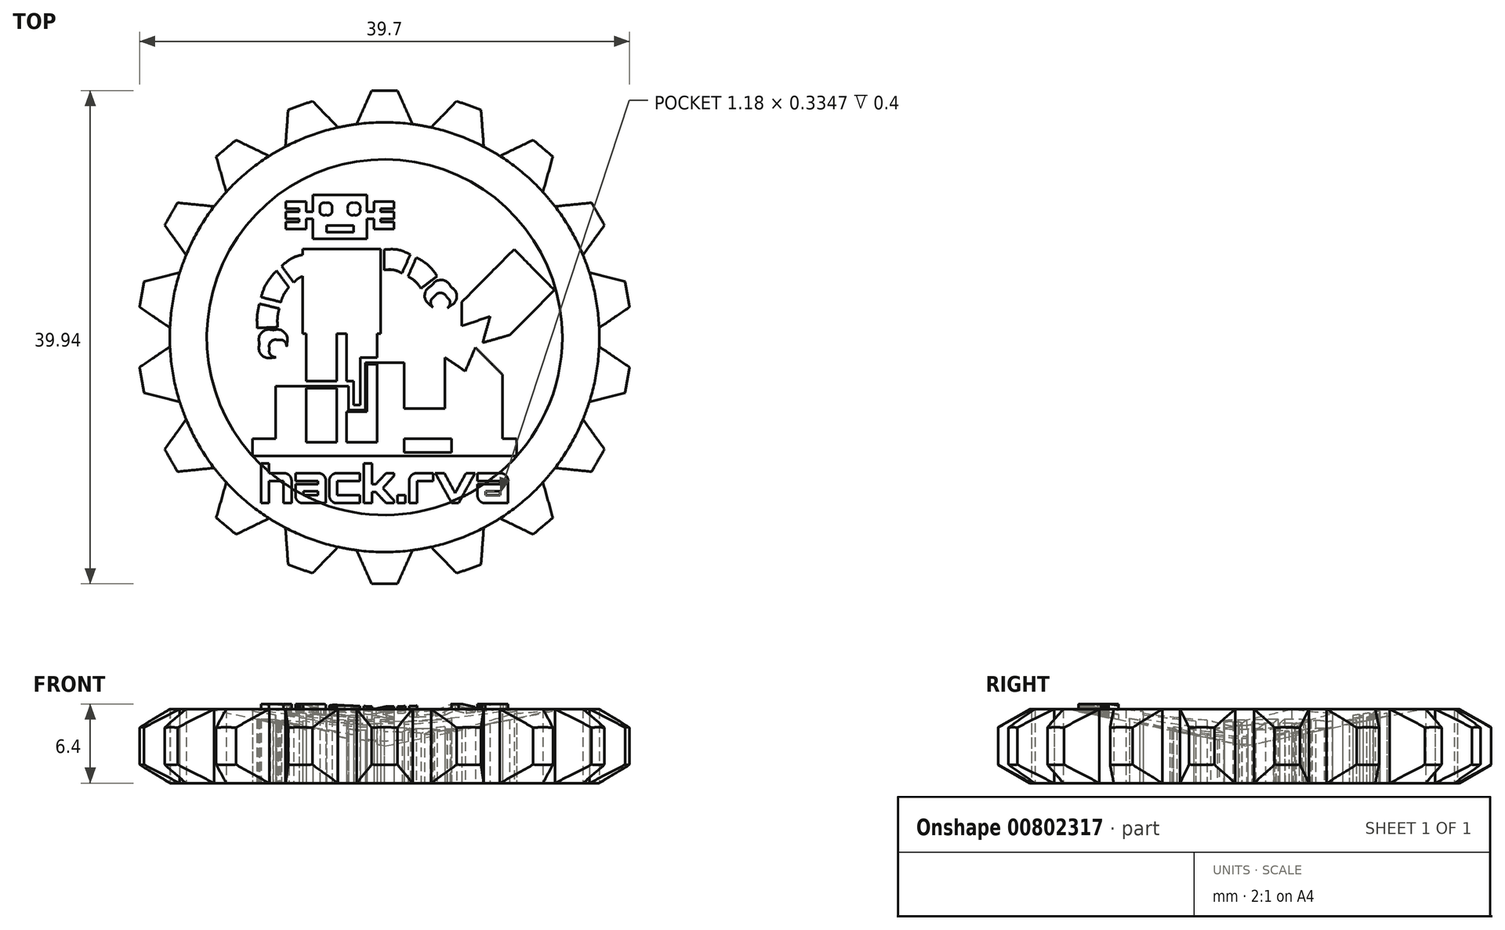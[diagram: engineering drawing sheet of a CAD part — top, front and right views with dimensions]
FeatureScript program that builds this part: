
annotation { "Feature Type Name" : "Feature", "Feature Type Description" : "" }
export const myFeature = defineFeature(function(context is Context, id is Id, definition is map)
    precondition{}
    {
        {
            var Q0;
            Q0=qCreatedBy(makeId("Top.planeOp"),FACE);
            var sketch = newSketch(context, id + "F0", { "sketchPlane" : qUnion([Q0])});
            skCircle(sketch, "E0", {"center": v(0, 0) * mm, "radius": 17.4 * mm, "construction": true});
            skCircle(sketch, "E1", {"center": v(0, 0) * mm, "radius": 20 * mm, "construction": true});
            skLineSegment(sketch, "E2", {"start": v(0, 0) * mm, "end": v(0, 27.02) * mm, "construction": true});
            skLineSegment(sketch, "E3", {"start": v(0, 0) * mm, "end": v(-2.84, 21.54) * mm, "construction": true});
            skLineSegment(sketch, "E4", {"start": v(0, 0) * mm, "end": v(-1.42, 27.06) * mm, "construction": true});
            skPoint(sketch, "E4.endSnap0", {"position": v(-1.42, 10.77) * mm});
            skLineSegment(sketch, "E5", {"start": v(-2.27, 17.25) * mm, "end": v(-1.05, 19.97) * mm});
            skLineSegment(sketch, "E6", {"start": v(-1.05, 19.97) * mm, "end": v(0, 19.97) * mm});
            skLineSegment(sketch, "E7.MirrorCS", {"start": v(2.27, 17.25) * mm, "end": v(1.05, 19.97) * mm});
            skLineSegment(sketch, "E8.MirrorCS", {"start": v(1.05, 19.97) * mm, "end": v(0, 19.97) * mm});
            skLineSegment(sketch, "E9", {"start": v(-2.27, 17.25) * mm, "end": v(2.27, 17.25) * mm});
            skSolve(sketch);
        }
        {
            var Q0;
            Q0=qCreatedBy(makeId("Top.planeOp"),FACE);
            var sketch = newSketch(context, id + "F1", { "sketchPlane" : qUnion([Q0])});
            skCircle(sketch, "E10", {"center": v(0, 0) * mm, "radius": 17.4 * mm});
            skSolve(sketch);
        }
        {
            var Q0;
            Q0 = qSketchRegion(id + "F1", true);
            var Q1;
            Q1 = qSketchRegion(id + "F0", true);
            extrude(context, id + "F2", {"entities" : qUnion([Q0, Q1]), "depth" : 6 * mm, "offsetDistance" : 25 * mm});
        }
        {
            var Q0;
            Q0=qCreatedBy(makeId("Front.planeOp"),FACE);
            var sketch = newSketch(context, id + "F3", { "sketchPlane" : qUnion([Q0])});
            skLineSegment(sketch, "E11", {"start": v(0, 0) * mm, "end": v(0, 3) * mm});
            skLineSegment(sketch, "E12", {"start": v(0, 3) * mm, "end": v(-14.4, 6) * mm});
            skLineSegment(sketch, "E13", {"start": v(-14.4, 6) * mm, "end": v(-17.4, 6) * mm});
            skLineSegment(sketch, "E14", {"start": v(-17.4, 6) * mm, "end": v(-20, 4.5) * mm});
            skLineSegment(sketch, "E15", {"start": v(-20, 4.5) * mm, "end": v(-20, 1.5) * mm});
            skLineSegment(sketch, "E16", {"start": v(-20, 1.5) * mm, "end": v(-17.4, 0) * mm});
            skLineSegment(sketch, "E17", {"start": v(-17.4, 0) * mm, "end": v(0, 0) * mm});
            skSolve(sketch);
        }
        {
            var Q0;
            Q0=makeQuery(id+"F2.opExtrude","SWEPT_BODY",BODY,{"disambiguationData":[OSD([sQuery(id+"F0.wireOp",EDGE,"E5"),sQuery(id+"F0.wireOp",EDGE,"E6"),sQuery(id+"F0.wireOp",EDGE,"E7.MirrorCS"),sQuery(id+"F0.wireOp",EDGE,"E8.MirrorCS"),sQuery(id+"F0.wireOp",EDGE,"E9")])]});
            var Q1;
            Q1=sQuery(id+"F3.wireOp",EDGE,"E11");
            circularPattern(context, id + "F4", {"operationType" : NewBodyOperationType.ADD, "entities" : qUnion([Q0]), "axis" : qUnion([Q1]), "angle" : 360 * degree, "instanceCount" : 18, "equalSpace" : true});
        }
        {
            var Q0;
            Q0=qCreatedBy(makeId("Top.planeOp"),FACE);
            var sketch = newSketch(context, id + "F5", { "sketchPlane" : qUnion([Q0])});
            skLineSegment(sketch, "E18", {"start": v(7.36, -0.83) * mm, "end": v(6.54, -2.75) * mm});
            skLineSegment(sketch, "E19", {"start": v(6.54, -2.75) * mm, "end": v(4.9, -1.65) * mm});
            skLineSegment(sketch, "E20", {"start": v(4.9, -1.65) * mm, "end": v(4.9, -9.06) * mm});
            skLineSegment(sketch, "E21", {"start": v(4.9, -9.06) * mm, "end": v(9.56, -9.06) * mm});
            skLineSegment(sketch, "E22", {"start": v(9.56, -9.06) * mm, "end": v(9.56, -3.02) * mm});
            skLineSegment(sketch, "E23", {"start": v(9.56, -3.02) * mm, "end": v(8.46, -1.92) * mm});
            skLineSegment(sketch, "E24", {"start": v(8.46, -1.92) * mm, "end": v(7.36, -0.83) * mm});
            skLineSegment(sketch, "E25", {"start": v(1.6, -5.77) * mm, "end": v(5.44, -5.77) * mm});
            skLineSegment(sketch, "E26", {"start": v(5.44, -5.77) * mm, "end": v(5.44, -9.33) * mm});
            skLineSegment(sketch, "E27", {"start": v(5.44, -9.33) * mm, "end": v(1.6, -9.33) * mm});
            skLineSegment(sketch, "E28", {"start": v(1.6, -9.33) * mm, "end": v(1.6, -5.77) * mm});
            skLineSegment(sketch, "E29", {"start": v(8.55, 1.69) * mm, "end": v(7.95, -0.45) * mm});
            skLineSegment(sketch, "E30", {"start": v(7.95, -0.45) * mm, "end": v(10.12, 0.17) * mm});
            skLineSegment(sketch, "E31", {"start": v(10.12, 0.17) * mm, "end": v(13.76, 3.82) * mm});
            skLineSegment(sketch, "E32", {"start": v(13.76, 3.82) * mm, "end": v(10.5, 7.12) * mm});
            skLineSegment(sketch, "E33", {"start": v(10.5, 7.12) * mm, "end": v(6.26, 2.85) * mm});
            skLineSegment(sketch, "E34", {"start": v(6.26, 2.85) * mm, "end": v(6.26, 0.9) * mm});
            skLineSegment(sketch, "E35", {"start": v(6.26, 0.9) * mm, "end": v(8.55, 1.69) * mm});
            skFitSpline(sketch, "E36", {"points": [v(-9.33, -0.94) * mm, v(-9.33, -0.55) * mm, v(-9.02, -0.23) * mm, v(-8.62, -0.23) * mm]});
            skFitSpline(sketch, "E37", {"points": [v(-8.62, -0.23) * mm, v(-8.3, -0.23) * mm, v(-8.02, -0.46) * mm, v(-7.94, -0.77) * mm]});
            skFitSpline(sketch, "E38", {"points": [v(-7.94, -0.77) * mm, v(-7.92, -0.7) * mm, v(-7.91, -0.61) * mm, v(-7.91, -0.53) * mm]});
            skFitSpline(sketch, "E39", {"points": [v(-7.91, -0.53) * mm, v(-7.91, 0.08) * mm, v(-8.41, 0.58) * mm, v(-9.03, 0.58) * mm]});
            skFitSpline(sketch, "E40", {"points": [v(-9.03, 0.58) * mm, v(-9.64, 0.58) * mm, v(-10.14, 0.08) * mm, v(-10.14, -0.53) * mm]});
            skFitSpline(sketch, "E41", {"points": [v(-10.14, -0.53) * mm, v(-10.14, -1.15) * mm, v(-9.64, -1.65) * mm, v(-9.03, -1.65) * mm]});
            skFitSpline(sketch, "E42", {"points": [v(-9.03, -1.65) * mm, v(-8.95, -1.65) * mm, v(-8.87, -1.64) * mm, v(-8.8, -1.63) * mm]});
            skFitSpline(sketch, "E43", {"points": [v(-8.8, -1.63) * mm, v(-9.1, -1.55) * mm, v(-9.33, -1.27) * mm, v(-9.33, -0.94) * mm]});
            skLineSegment(sketch, "E44", {"start": v(-1.42, 10.15) * mm, "end": v(0.77, 10.15) * mm});
            skLineSegment(sketch, "E45", {"start": v(0.77, 10.15) * mm, "end": v(0.77, 9.6) * mm});
            skLineSegment(sketch, "E46", {"start": v(0.77, 9.6) * mm, "end": v(-1.42, 9.6) * mm});
            skLineSegment(sketch, "E47", {"start": v(-1.42, 9.6) * mm, "end": v(-1.42, 10.15) * mm});
            skFitSpline(sketch, "E48", {"points": [v(4.04, 3.29) * mm, v(4.33, 3.55) * mm, v(4.78, 3.53) * mm, v(5.04, 3.24) * mm]});
            skFitSpline(sketch, "E49", {"points": [v(5.04, 3.24) * mm, v(5.27, 3) * mm, v(5.29, 2.64) * mm, v(5.11, 2.38) * mm]});
            skFitSpline(sketch, "E50", {"points": [v(5.11, 2.38) * mm, v(5.18, 2.42) * mm, v(5.24, 2.46) * mm, v(5.3, 2.51) * mm]});
            skFitSpline(sketch, "E51", {"points": [v(5.3, 2.51) * mm, v(5.75, 2.93) * mm, v(5.79, 3.64) * mm, v(5.37, 4.1) * mm]});
            skFitSpline(sketch, "E52", {"points": [v(5.37, 4.1) * mm, v(4.95, 4.55) * mm, v(4.25, 4.58) * mm, v(3.8, 4.16) * mm]});
            skFitSpline(sketch, "E53", {"points": [v(3.8, 4.16) * mm, v(3.34, 3.75) * mm, v(3.3, 3.04) * mm, v(3.72, 2.58) * mm]});
            skFitSpline(sketch, "E54", {"points": [v(3.72, 2.58) * mm, v(3.78, 2.53) * mm, v(3.84, 2.48) * mm, v(3.9, 2.43) * mm]});
            skFitSpline(sketch, "E55", {"points": [v(3.9, 2.43) * mm, v(3.75, 2.71) * mm, v(3.8, 3.07) * mm, v(4.04, 3.29) * mm]});
            skFitSpline(sketch, "E56", {"points": [v(-5.24, 10.39) * mm, v(-5.24, 10.65) * mm, v(-5.02, 10.87) * mm, v(-4.75, 10.87) * mm]});
            skFitSpline(sketch, "E57", {"points": [v(-4.75, 10.87) * mm, v(-4.48, 10.87) * mm, v(-4.26, 10.65) * mm, v(-4.26, 10.39) * mm]});
            skFitSpline(sketch, "E58", {"points": [v(-4.26, 10.39) * mm, v(-4.26, 10.12) * mm, v(-4.48, 9.9) * mm, v(-4.75, 9.9) * mm]});
            skFitSpline(sketch, "E59", {"points": [v(-4.75, 9.9) * mm, v(-5.02, 9.9) * mm, v(-5.24, 10.12) * mm, v(-5.24, 10.39) * mm]});
            skLineSegment(sketch, "E60", {"start": v(-5.81, 11.52) * mm, "end": v(-5.81, 7.95) * mm});
            skLineSegment(sketch, "E61", {"start": v(-5.81, 7.95) * mm, "end": v(-1.42, 7.95) * mm});
            skLineSegment(sketch, "E62", {"start": v(-1.42, 7.95) * mm, "end": v(-1.42, 11.52) * mm});
            skLineSegment(sketch, "E63", {"start": v(-1.42, 11.52) * mm, "end": v(-5.81, 11.52) * mm});
            skFitSpline(sketch, "E64", {"points": [v(-2.48, 9.9) * mm, v(-2.75, 9.9) * mm, v(-2.97, 10.12) * mm, v(-2.97, 10.39) * mm]});
            skFitSpline(sketch, "E65", {"points": [v(-2.97, 10.39) * mm, v(-2.97, 10.65) * mm, v(-2.75, 10.87) * mm, v(-2.48, 10.87) * mm]});
            skFitSpline(sketch, "E66", {"points": [v(-2.48, 10.87) * mm, v(-2.21, 10.87) * mm, v(-2, 10.65) * mm, v(-2, 10.39) * mm]});
            skFitSpline(sketch, "E67", {"points": [v(-2, 10.39) * mm, v(-2, 10.12) * mm, v(-2.21, 9.9) * mm, v(-2.48, 9.9) * mm]});
            skLineSegment(sketch, "E68", {"start": v(-2.52, 8.5) * mm, "end": v(-4.71, 8.5) * mm});
            skLineSegment(sketch, "E69", {"start": v(-4.71, 8.5) * mm, "end": v(-4.71, 9.05) * mm});
            skLineSegment(sketch, "E70", {"start": v(-4.71, 9.05) * mm, "end": v(-2.52, 9.05) * mm});
            skLineSegment(sketch, "E71", {"start": v(-2.52, 9.05) * mm, "end": v(-2.52, 8.5) * mm});
            skLineSegment(sketch, "E72", {"start": v(0.77, 8.78) * mm, "end": v(-0.87, 8.78) * mm});
            skLineSegment(sketch, "E73", {"start": v(-0.87, 8.78) * mm, "end": v(-0.87, 10.97) * mm});
            skLineSegment(sketch, "E74", {"start": v(-0.87, 10.97) * mm, "end": v(0.77, 10.97) * mm});
            skLineSegment(sketch, "E75", {"start": v(0.77, 10.97) * mm, "end": v(0.77, 10.42) * mm});
            skLineSegment(sketch, "E76", {"start": v(0.77, 10.42) * mm, "end": v(-0.32, 10.42) * mm});
            skLineSegment(sketch, "E77", {"start": v(-0.32, 10.42) * mm, "end": v(-0.32, 9.33) * mm});
            skLineSegment(sketch, "E78", {"start": v(-0.32, 9.33) * mm, "end": v(0.77, 9.33) * mm});
            skLineSegment(sketch, "E79", {"start": v(0.77, 9.33) * mm, "end": v(0.77, 8.78) * mm});
            skLineSegment(sketch, "E80", {"start": v(-8, 10.15) * mm, "end": v(-5.81, 10.15) * mm});
            skLineSegment(sketch, "E81", {"start": v(-5.81, 10.15) * mm, "end": v(-5.81, 9.6) * mm});
            skLineSegment(sketch, "E82", {"start": v(-5.81, 9.6) * mm, "end": v(-8, 9.6) * mm});
            skLineSegment(sketch, "E83", {"start": v(-8, 9.6) * mm, "end": v(-8, 10.15) * mm});
            skLineSegment(sketch, "E84", {"start": v(-6.36, 8.78) * mm, "end": v(-8, 8.78) * mm});
            skLineSegment(sketch, "E85", {"start": v(-8, 8.78) * mm, "end": v(-8, 9.33) * mm});
            skLineSegment(sketch, "E86", {"start": v(-8, 9.33) * mm, "end": v(-6.9, 9.33) * mm});
            skLineSegment(sketch, "E87", {"start": v(-6.9, 9.33) * mm, "end": v(-6.9, 10.42) * mm});
            skLineSegment(sketch, "E88", {"start": v(-6.9, 10.42) * mm, "end": v(-8, 10.42) * mm});
            skLineSegment(sketch, "E89", {"start": v(-8, 10.42) * mm, "end": v(-8, 10.97) * mm});
            skLineSegment(sketch, "E90", {"start": v(-8, 10.97) * mm, "end": v(-6.36, 10.97) * mm});
            skLineSegment(sketch, "E91", {"start": v(-6.36, 10.97) * mm, "end": v(-6.36, 8.78) * mm});
            skLineSegment(sketch, "E92", {"start": v(-6.63, 7.13) * mm, "end": v(-0.32, 7.13) * mm});
            skLineSegment(sketch, "E93", {"start": v(-0.32, 7.13) * mm, "end": v(-0.32, 0.27) * mm});
            skLineSegment(sketch, "E94", {"start": v(-0.32, 0.27) * mm, "end": v(-6.63, 0.27) * mm});
            skLineSegment(sketch, "E95", {"start": v(-6.63, 0.27) * mm, "end": v(-6.63, 7.13) * mm});
            skFitSpline(sketch, "E96", {"points": [v(1.9, 4.93) * mm, v(2.29, 4.69) * mm, v(2.64, 4.36) * mm, v(2.95, 3.95) * mm]});
            skLineSegment(sketch, "E97", {"start": v(2.58, 6.45) * mm, "end": v(1.9, 4.93) * mm});
            skLineSegment(sketch, "E98", {"start": v(1.9, 4.93) * mm, "end": v(2.58, 6.45) * mm});
            skFitSpline(sketch, "E99", {"points": [v(4.26, 4.95) * mm, v(3.78, 5.59) * mm, v(3.2, 6.1) * mm, v(2.58, 6.45) * mm]});
            skLineSegment(sketch, "E100", {"start": v(2.95, 3.95) * mm, "end": v(4.26, 4.95) * mm});
            skLineSegment(sketch, "E101", {"start": v(4.26, 4.95) * mm, "end": v(2.95, 3.95) * mm});
            skFitSpline(sketch, "E102", {"points": [v(-5.82, 6.69) * mm, v(-6.77, 6.65) * mm, v(-7.63, 6.32) * mm, v(-8.34, 5.76) * mm]});
            skFitSpline(sketch, "E103", {"points": [v(-7.37, 4.43) * mm, v(-6.91, 4.8) * mm, v(-6.37, 5.02) * mm, v(-5.75, 5.04) * mm]});
            skFitSpline(sketch, "E104", {"points": [v(-5.75, 5.04) * mm, v(-4.6, 5.1) * mm, v(-3.52, 4.48) * mm, v(-2.78, 3.35) * mm]});
            skLineSegment(sketch, "E105", {"start": v(-8.34, 5.76) * mm, "end": v(-7.37, 4.43) * mm});
            skLineSegment(sketch, "E106", {"start": v(-7.37, 4.43) * mm, "end": v(-8.34, 5.76) * mm});
            skFitSpline(sketch, "E107", {"points": [v(-1.4, 4.25) * mm, v(-2.47, 5.88) * mm, v(-4.08, 6.77) * mm, v(-5.82, 6.69) * mm]});
            skLineSegment(sketch, "E108", {"start": v(-2.78, 3.35) * mm, "end": v(-1.4, 4.25) * mm});
            skLineSegment(sketch, "E109", {"start": v(-1.4, 4.25) * mm, "end": v(-2.78, 3.35) * mm});
            skFitSpline(sketch, "E110", {"points": [v(-10.14, 2.71) * mm, v(-10.28, 2.1) * mm, v(-10.34, 1.43) * mm, v(-10.3, 0.74) * mm]});
            skLineSegment(sketch, "E111", {"start": v(-8.54, 2.32) * mm, "end": v(-10.14, 2.71) * mm});
            skLineSegment(sketch, "E112", {"start": v(-10.14, 2.71) * mm, "end": v(-8.54, 2.32) * mm});
            skFitSpline(sketch, "E113", {"points": [v(-8.66, 0.82) * mm, v(-8.69, 1.35) * mm, v(-8.64, 1.85) * mm, v(-8.54, 2.32) * mm]});
            skLineSegment(sketch, "E114", {"start": v(-10.3, 0.74) * mm, "end": v(-8.66, 0.82) * mm});
            skLineSegment(sketch, "E115", {"start": v(-8.66, 0.82) * mm, "end": v(-10.3, 0.74) * mm});
            skFitSpline(sketch, "E116", {"points": [v(-8.4, 2.85) * mm, v(-8.28, 3.22) * mm, v(-8.12, 3.55) * mm, v(-7.92, 3.84) * mm]});
            skFitSpline(sketch, "E117", {"points": [v(-7.92, 3.84) * mm, v(-7.87, 3.9) * mm, v(-7.81, 3.98) * mm, v(-7.76, 4.04) * mm]});
            skFitSpline(sketch, "E118", {"points": [v(-8.75, 5.39) * mm, v(-8.94, 5.2) * mm, v(-9.11, 5) * mm, v(-9.27, 4.78) * mm]});
            skFitSpline(sketch, "E119", {"points": [v(-9.27, 4.78) * mm, v(-9.58, 4.32) * mm, v(-9.82, 3.8) * mm, v(-10, 3.24) * mm]});
            skLineSegment(sketch, "E120", {"start": v(-7.76, 4.04) * mm, "end": v(-8.75, 5.39) * mm});
            skLineSegment(sketch, "E121", {"start": v(-8.75, 5.39) * mm, "end": v(-7.76, 4.04) * mm});
            skLineSegment(sketch, "E122", {"start": v(-10, 3.24) * mm, "end": v(-8.4, 2.85) * mm});
            skLineSegment(sketch, "E123", {"start": v(-8.4, 2.85) * mm, "end": v(-10, 3.24) * mm});
            skLineSegment(sketch, "E124", {"start": v(1.6, -2.05) * mm, "end": v(-1.57, -2.05) * mm});
            skLineSegment(sketch, "E125", {"start": v(-2.52, -3.57) * mm, "end": v(-2.52, -5.5) * mm});
            skLineSegment(sketch, "E126", {"start": v(-2.52, -5.5) * mm, "end": v(-1.97, -5.5) * mm});
            skLineSegment(sketch, "E127", {"start": v(-0.6, -1.65) * mm, "end": v(-0.6, 1.1) * mm});
            skLineSegment(sketch, "E128", {"start": v(-0.6, 1.1) * mm, "end": v(-3.07, 1.1) * mm});
            skLineSegment(sketch, "E129", {"start": v(-3.07, 1.1) * mm, "end": v(-3.07, -3.57) * mm});
            skLineSegment(sketch, "E130", {"start": v(-3.07, -3.57) * mm, "end": v(-2.52, -3.57) * mm});
            skLineSegment(sketch, "E131", {"start": v(-0.6, -2.2) * mm, "end": v(-1.42, -2.2) * mm});
            skLineSegment(sketch, "E132", {"start": v(-1.42, -2.2) * mm, "end": v(-1.42, -6.04) * mm});
            skLineSegment(sketch, "E133", {"start": v(-1.42, -6.04) * mm, "end": v(-3.07, -6.04) * mm});
            skLineSegment(sketch, "E134", {"start": v(-3.07, -6.04) * mm, "end": v(-3.07, -8.5) * mm});
            skLineSegment(sketch, "E135", {"start": v(-3.07, -8.5) * mm, "end": v(-1.15, -8.5) * mm});
            skLineSegment(sketch, "E136", {"start": v(-1.15, -8.5) * mm, "end": v(-0.6, -8.5) * mm});
            skLineSegment(sketch, "E137", {"start": v(-0.6, -8.5) * mm, "end": v(-0.6, -2.2) * mm});
            skLineSegment(sketch, "E138", {"start": v(-10.7, -8.23) * mm, "end": v(10.7, -8.23) * mm});
            skLineSegment(sketch, "E139", {"start": v(10.7, -9.6) * mm, "end": v(-10.7, -9.6) * mm});
            skFitSpline(sketch, "E140", {"points": [v(-0.05, 5.44) * mm, v(0.45, 5.48) * mm, v(0.95, 5.4) * mm, v(1.42, 5.2) * mm]});
            skLineSegment(sketch, "E141", {"start": v(-0.05, 7.09) * mm, "end": v(-0.05, 5.44) * mm});
            skLineSegment(sketch, "E142", {"start": v(-0.05, 5.44) * mm, "end": v(-0.05, 7.09) * mm});
            skFitSpline(sketch, "E143", {"points": [v(2.09, 6.7) * mm, v(1.41, 7) * mm, v(0.7, 7.13) * mm, v(-0.05, 7.09) * mm]});
            skLineSegment(sketch, "E144", {"start": v(1.42, 5.2) * mm, "end": v(2.09, 6.7) * mm});
            skLineSegment(sketch, "E145", {"start": v(2.09, 6.7) * mm, "end": v(1.42, 5.2) * mm});
            skLineSegment(sketch, "E146", {"start": v(-6.36, 1.1) * mm, "end": v(-3.89, 1.1) * mm});
            skLineSegment(sketch, "E147", {"start": v(-3.89, 1.1) * mm, "end": v(-3.89, -3.57) * mm});
            skLineSegment(sketch, "E148", {"start": v(-3.89, -3.57) * mm, "end": v(-6.36, -3.57) * mm});
            skLineSegment(sketch, "E149", {"start": v(-6.36, -3.57) * mm, "end": v(-6.36, 1.1) * mm});
            skLineSegment(sketch, "E150", {"start": v(-6.36, -4.12) * mm, "end": v(-3.89, -4.12) * mm});
            skLineSegment(sketch, "E151", {"start": v(-3.89, -4.12) * mm, "end": v(-3.89, -8.5) * mm});
            skLineSegment(sketch, "E152", {"start": v(-3.89, -8.5) * mm, "end": v(-6.36, -8.5) * mm});
            skLineSegment(sketch, "E153", {"start": v(-6.36, -8.5) * mm, "end": v(-6.36, -4.12) * mm});
            skLineSegment(sketch, "E154", {"start": v(10.7, -8.23) * mm, "end": v(10.7, -9.6) * mm});
            skLineSegment(sketch, "E155", {"start": v(-10.7, -9.6) * mm, "end": v(-10.7, -8.23) * mm});
            skLineSegment(sketch, "E156", {"start": v(-1.57, -2.05) * mm, "end": v(-1.57, -5.9) * mm});
            skLineSegment(sketch, "E157", {"start": v(-1.97, -1.65) * mm, "end": v(-1.97, -5.5) * mm});
            skLineSegment(sketch, "E158", {"start": v(1.6, -2.05) * mm, "end": v(1.6, -8.78) * mm});
            skLineSegment(sketch, "E159", {"start": v(1.6, -8.78) * mm, "end": v(-0.87, -8.78) * mm});
            skLineSegment(sketch, "E160", {"start": v(-0.87, -8.78) * mm, "end": v(-0.87, -9.33) * mm});
            skLineSegment(sketch, "E161", {"start": v(-0.87, -9.33) * mm, "end": v(-2.8, -9.33) * mm});
            skLineSegment(sketch, "E162", {"start": v(-2.8, -9.33) * mm, "end": v(-2.8, -9.6) * mm});
            skLineSegment(sketch, "E163", {"start": v(-2.8, -9.6) * mm, "end": v(-8.83, -9.6) * mm});
            skLineSegment(sketch, "E164", {"start": v(-8.83, -9.6) * mm, "end": v(-8.83, -3.97) * mm});
            skLineSegment(sketch, "E165", {"start": v(-0.6, -1.65) * mm, "end": v(-1.97, -1.65) * mm});
            skLineSegment(sketch, "E166", {"start": v(-2.92, -5.9) * mm, "end": v(-1.57, -5.9) * mm});
            skLineSegment(sketch, "E167", {"start": v(-2.92, -3.97) * mm, "end": v(-2.92, -5.9) * mm});
            skLineSegment(sketch, "E168", {"start": v(-2.92, -3.97) * mm, "end": v(-8.83, -3.97) * mm});
            skSolve(sketch);
        }
        {
            var Q0;
            Q0 = qSketchRegion(id + "F5", true);
            var Q1;
            Q1=sQuery(id+"F5.wireOp",EDGE,"E134");
            var Q2;
            Q2=sQuery(id+"F5.wireOp",EDGE,"E94");
            var Q3;
            Q3=sQuery(id+"F5.wireOp",EDGE,"E148");
            var Q4;
            Q4=sQuery(id+"F5.wireOp",EDGE,"E99");
            var Q5;
            Q5=sQuery(id+"F5.wireOp",EDGE,"E143");
            var Q6;
            Q6=sQuery(id+"F5.wireOp",EDGE,"E22");
            var Q7;
            Q7=sQuery(id+"F5.wireOp",EDGE,"E35");
            var Q8;
            Q8=sQuery(id+"F5.wireOp",EDGE,"E28");
            var Q9;
            Q9=sQuery(id+"F5.wireOp",EDGE,"E110");
            var Q10;
            Q10=sQuery(id+"F5.wireOp",EDGE,"95198ed3-3c3b-4ae5-9471-770df729d098");
            var Q11;
            Q11=sQuery(id+"F5.wireOp",EDGE,"E149");
            var Q12;
            Q12=sQuery(id+"F5.wireOp",EDGE,"E137");
            var Q13;
            Q13=sQuery(id+"F5.wireOp",EDGE,"E26");
            var Q14;
            Q14=sQuery(id+"F5.wireOp",EDGE,"E104");
            var Q15;
            Q15=sQuery(id+"F5.wireOp",EDGE,"E20");
            var Q16;
            Q16=sQuery(id+"F5.wireOp",EDGE,"E68");
            var Q17;
            Q17=sQuery(id+"F5.wireOp",EDGE,"E138");
            var Q18;
            Q18=sQuery(id+"F5.wireOp",EDGE,"E129");
            var Q19;
            Q19=sQuery(id+"F5.wireOp",EDGE,"77c6bc89-9393-4709-9f76-2ba73c08c8e3");
            var Q20;
            Q20=sQuery(id+"F5.wireOp",EDGE,"E34");
            var Q21;
            Q21=sQuery(id+"F5.wireOp",EDGE,"E147");
            var Q22;
            Q22=sQuery(id+"F5.wireOp",EDGE,"b3271c8d-d34e-48d3-8350-166866a1ef0d");
            var Q23;
            Q23=sQuery(id+"F5.wireOp",EDGE,"E33");
            var Q24;
            Q24=sQuery(id+"F5.wireOp",EDGE,"E152");
            var Q25;
            Q25=sQuery(id+"F5.wireOp",EDGE,"E21");
            var Q26;
            Q26=sQuery(id+"F5.wireOp",EDGE,"9cf7919e-c9ea-4169-a484-167db1e63cf2");
            var Q27;
            Q27=sQuery(id+"F5.wireOp",EDGE,"E70");
            var Q28;
            Q28=sQuery(id+"F5.wireOp",EDGE,"E18");
            var Q29;
            Q29=sQuery(id+"F5.wireOp",EDGE,"E31");
            var Q30;
            Q30=sQuery(id+"F5.wireOp",EDGE,"E32");
            var Q31;
            Q31=sQuery(id+"F5.wireOp",EDGE,"E27");
            var Q32;
            Q32=sQuery(id+"F5.wireOp",EDGE,"E30");
            var Q33;
            Q33=sQuery(id+"F5.wireOp",EDGE,"E29");
            var Q34;
            Q34=sQuery(id+"F5.wireOp",EDGE,"E153");
            var Q35;
            Q35=sQuery(id+"F5.wireOp",EDGE,"E107");
            var Q36;
            Q36=sQuery(id+"F5.wireOp",EDGE,"E127");
            var Q37;
            Q37=sQuery(id+"F5.wireOp",EDGE,"E124");
            var Q38;
            Q38=sQuery(id+"F5.wireOp",EDGE,"E92");
            var Q39;
            Q39=sQuery(id+"F5.wireOp",EDGE,"E150");
            var Q40;
            Q40=sQuery(id+"F5.wireOp",EDGE,"E102");
            var Q41;
            Q41=sQuery(id+"F5.wireOp",EDGE,"1cbca8c9-4c5e-4ba1-ad6a-0479403318c5");
            var Q42;
            Q42=sQuery(id+"F5.wireOp",EDGE,"E151");
            var Q43;
            Q43=sQuery(id+"F5.wireOp",EDGE,"E25");
            var Q44;
            Q44=sQuery(id+"F5.wireOp",EDGE,"E146");
            var Q45;
            Q45=sQuery(id+"F5.wireOp",EDGE,"E132");
            var Q46;
            Q46=sQuery(id+"F5.wireOp",EDGE,"9599e65c-5a11-434d-bada-090ac9876402");
            var Q47;
            Q47=sQuery(id+"F5.wireOp",EDGE,"E63");
            var Q48;
            Q48=sQuery(id+"F5.wireOp",EDGE,"E95");
            var Q49;
            Q49=sQuery(id+"F5.wireOp",EDGE,"3e5a58c2-594a-425e-9fb5-5e991799c867");
            var Q50;
            Q50=sQuery(id+"F5.wireOp",EDGE,"E93");
            var Q51;
            Q51=sQuery(id+"F5.wireOp",EDGE,"E61");
            var Q52;
            Q52=sQuery(id+"F5.wireOp",EDGE,"E128");
            var Q53;
            Q53=sQuery(id+"F5.wireOp",EDGE,"E139");
            var Q54;
            Q54=sQuery(id+"F5.wireOp",EDGE,"9c611efc-dcd8-4982-9a14-8ccc37464665");
            var Q55;
            Q55=sQuery(id+"F5.wireOp",EDGE,"E135");
            var Q56;
            Q56=sQuery(id+"F5.wireOp",EDGE,"E67");
            var Q57;
            Q57=sQuery(id+"F5.wireOp",EDGE,"a202889e-5133-40a2-9648-54841ea52ae1");
            var Q58;
            Q58=sQuery(id+"F5.wireOp",EDGE,"E51");
            var Q59;
            Q59=sQuery(id+"F5.wireOp",EDGE,"E52");
            var Q60;
            Q60=sQuery(id+"F5.wireOp",EDGE,"E23");
            var Q61;
            Q61=sQuery(id+"F5.wireOp",EDGE,"245d8472-72b8-4d4c-ba14-2023b326ec3c");
            var Q62;
            Q62=sQuery(id+"F5.wireOp",EDGE,"E37");
            var Q63;
            Q63=sQuery(id+"F5.wireOp",EDGE,"E40");
            var Q64;
            Q64=sQuery(id+"F5.wireOp",EDGE,"E88");
            var Q65;
            Q65=sQuery(id+"F5.wireOp",EDGE,"E56");
            var Q66;
            Q66=sQuery(id+"F5.wireOp",EDGE,"E125");
            var Q67;
            Q67=sQuery(id+"F5.wireOp",EDGE,"9350a63d-57cb-49f3-a7ef-09ff34bb147e");
            var Q68;
            Q68=sQuery(id+"F5.wireOp",EDGE,"E75");
            var Q69;
            Q69=sQuery(id+"F5.wireOp",EDGE,"E38");
            var Q70;
            Q70=sQuery(id+"F5.wireOp",EDGE,"E36");
            var Q71;
            Q71=sQuery(id+"F5.wireOp",EDGE,"E19");
            var Q72;
            Q72=sQuery(id+"F5.wireOp",EDGE,"E119");
            var Q73;
            Q73=sQuery(id+"F5.wireOp",EDGE,"E64");
            var Q74;
            Q74=sQuery(id+"F5.wireOp",EDGE,"7eb34144-0e09-40d5-ad89-3aa24f313f34");
            var Q75;
            Q75=sQuery(id+"F5.wireOp",EDGE,"E62");
            var Q76;
            Q76=sQuery(id+"F5.wireOp",EDGE,"E131");
            var Q77;
            Q77=sQuery(id+"F5.wireOp",EDGE,"E66");
            var Q78;
            Q78=sQuery(id+"F5.wireOp",EDGE,"E103");
            var Q79;
            Q79=sQuery(id+"F5.wireOp",EDGE,"E39");
            var Q80;
            Q80=sQuery(id+"F5.wireOp",EDGE,"E24");
            var Q81;
            Q81=sQuery(id+"F5.wireOp",EDGE,"271be0f0-f1cb-4401-a4b2-863b38b25cbf");
            var Q82;
            Q82=sQuery(id+"F5.wireOp",EDGE,"E59");
            var Q83;
            Q83=sQuery(id+"F5.wireOp",EDGE,"E58");
            var Q84;
            Q84=sQuery(id+"F5.wireOp",EDGE,"6881dcda-d3f3-45b8-92d9-aef02fdce9f0");
            var Q85;
            Q85=sQuery(id+"F5.wireOp",EDGE,"E76");
            var Q86;
            Q86=sQuery(id+"F5.wireOp",EDGE,"E60");
            var Q87;
            Q87=sQuery(id+"F5.wireOp",EDGE,"E133");
            var Q88;
            Q88=sQuery(id+"F5.wireOp",EDGE,"E50");
            var Q89;
            Q89=sQuery(id+"F5.wireOp",EDGE,"E65");
            var Q90;
            Q90=sQuery(id+"F5.wireOp",EDGE,"E48");
            var Q91;
            Q91=sQuery(id+"F5.wireOp",EDGE,"E77");
            var Q92;
            Q92=sQuery(id+"F5.wireOp",EDGE,"E90");
            var Q93;
            Q93=sQuery(id+"F5.wireOp",EDGE,"E74");
            var Q94;
            Q94=sQuery(id+"F5.wireOp",EDGE,"E126");
            var Q95;
            Q95=sQuery(id+"F5.wireOp",EDGE,"E41");
            var Q96;
            Q96=sQuery(id+"F5.wireOp",EDGE,"E57");
            var Q97;
            Q97=sQuery(id+"F5.wireOp",EDGE,"E73");
            var Q98;
            Q98=sQuery(id+"F5.wireOp",EDGE,"E123");
            var Q99;
            Q99=sQuery(id+"F5.wireOp",EDGE,"E140");
            var Q100;
            Q100=sQuery(id+"F5.wireOp",EDGE,"E136");
            var Q101;
            Q101=sQuery(id+"F5.wireOp",EDGE,"E145");
            var Q102;
            Q102=sQuery(id+"F5.wireOp",EDGE,"E112");
            var Q103;
            Q103=sQuery(id+"F5.wireOp",EDGE,"E113");
            var Q104;
            Q104=sQuery(id+"F5.wireOp",EDGE,"E49");
            var Q105;
            Q105=sQuery(id+"F5.wireOp",EDGE,"E115");
            var Q106;
            Q106=sQuery(id+"F5.wireOp",EDGE,"E101");
            var Q107;
            Q107=sQuery(id+"F5.wireOp",EDGE,"E87");
            var Q108;
            Q108=sQuery(id+"F5.wireOp",EDGE,"E120");
            var Q109;
            Q109=sQuery(id+"F5.wireOp",EDGE,"E106");
            var Q110;
            Q110=sQuery(id+"F5.wireOp",EDGE,"E44");
            var Q111;
            Q111=sQuery(id+"F5.wireOp",EDGE,"E53");
            var Q112;
            Q112=sQuery(id+"F5.wireOp",EDGE,"E117");
            var Q113;
            Q113=sQuery(id+"F5.wireOp",EDGE,"bea348f1-2834-486b-88b8-9efe3fc24a35");
            var Q114;
            Q114=sQuery(id+"F5.wireOp",EDGE,"E118");
            var Q115;
            Q115=sQuery(id+"F5.wireOp",EDGE,"E116");
            var Q116;
            Q116=sQuery(id+"F5.wireOp",EDGE,"E98");
            var Q117;
            Q117=sQuery(id+"F5.wireOp",EDGE,"E96");
            var Q118;
            Q118=sQuery(id+"F5.wireOp",EDGE,"E109");
            var Q119;
            Q119=sQuery(id+"F5.wireOp",EDGE,"E142");
            var Q120;
            Q120=sQuery(id+"F5.wireOp",EDGE,"E83");
            var Q121;
            Q121=sQuery(id+"F5.wireOp",EDGE,"E84");
            var Q122;
            Q122=sQuery(id+"F5.wireOp",EDGE,"E144");
            var Q123;
            Q123=sQuery(id+"F5.wireOp",EDGE,"E80");
            var Q124;
            Q124=sQuery(id+"F5.wireOp",EDGE,"E97");
            var Q125;
            Q125=sQuery(id+"F5.wireOp",EDGE,"E71");
            var Q126;
            Q126=sQuery(id+"F5.wireOp",EDGE,"E72");
            var Q127;
            Q127=sQuery(id+"F5.wireOp",EDGE,"E100");
            var Q128;
            Q128=sQuery(id+"F5.wireOp",EDGE,"E111");
            var Q129;
            Q129=sQuery(id+"F5.wireOp",EDGE,"E78");
            var Q130;
            Q130=sQuery(id+"F5.wireOp",EDGE,"E46");
            var Q131;
            Q131=sQuery(id+"F5.wireOp",EDGE,"E81");
            var Q132;
            Q132=sQuery(id+"F5.wireOp",EDGE,"E114");
            var Q133;
            Q133=sQuery(id+"F5.wireOp",EDGE,"E85");
            var Q134;
            Q134=sQuery(id+"F5.wireOp",EDGE,"E55");
            var Q135;
            Q135=sQuery(id+"F5.wireOp",EDGE,"E122");
            var Q136;
            Q136=sQuery(id+"F5.wireOp",EDGE,"E108");
            var Q137;
            Q137=sQuery(id+"F5.wireOp",EDGE,"E141");
            var Q138;
            Q138=sQuery(id+"F5.wireOp",EDGE,"E69");
            var Q139;
            Q139=sQuery(id+"F5.wireOp",EDGE,"E86");
            var Q140;
            Q140=sQuery(id+"F5.wireOp",EDGE,"E82");
            var Q141;
            Q141=sQuery(id+"F5.wireOp",EDGE,"E130");
            var Q142;
            Q142=sQuery(id+"F5.wireOp",EDGE,"E47");
            var Q143;
            Q143=sQuery(id+"F5.wireOp",EDGE,"E79");
            var Q144;
            Q144=sQuery(id+"F5.wireOp",EDGE,"E45");
            var Q145;
            Q145=sQuery(id+"F5.wireOp",EDGE,"E91");
            var Q146;
            Q146=sQuery(id+"F5.wireOp",EDGE,"E43");
            var Q147;
            Q147=sQuery(id+"F5.wireOp",EDGE,"E89");
            var Q148;
            Q148=sQuery(id+"F5.wireOp",EDGE,"E105");
            var Q149;
            Q149=sQuery(id+"F5.wireOp",EDGE,"E121");
            var Q150;
            Q150=sQuery(id+"F5.wireOp",EDGE,"E54");
            var Q151;
            Q151=sQuery(id+"F5.wireOp",EDGE,"E42");
            extrude(context, id + "F6", {"entities" : qUnion([Q0]), "operationType" : NewBodyOperationType.REMOVE, "surfaceEntities" : qUnion([Q1, Q2, Q3, Q4, Q5, Q6, Q7, Q8, Q9, Q10, Q11, Q12, Q13, Q14, Q15, Q16, Q17, Q18, Q19, Q20, Q21, Q22, Q23, Q24, Q25, Q26, Q27, Q28, Q29, Q30, Q31, Q32, Q33, Q34, Q35, Q36, Q37, Q38, Q39, Q40, Q41, Q42, Q43, Q44, Q45, Q46, Q47, Q48, Q49, Q50, Q51, Q52, Q53, Q54, Q55, Q56, Q57, Q58, Q59, Q60, Q61, Q62, Q63, Q64, Q65, Q66, Q67, Q68, Q69, Q70, Q71, Q72, Q73, Q74, Q75, Q76, Q77, Q78, Q79, Q80, Q81, Q82, Q83, Q84, Q85, Q86, Q87, Q88, Q89, Q90, Q91, Q92, Q93, Q94, Q95, Q96, Q97, Q98, Q99, Q100, Q101, Q102, Q103, Q104, Q105, Q106, Q107, Q108, Q109, Q110, Q111, Q112, Q113, Q114, Q115, Q116, Q117, Q118, Q119, Q120, Q121, Q122, Q123, Q124, Q125, Q126, Q127, Q128, Q129, Q130, Q131, Q132, Q133, Q134, Q135, Q136, Q137, Q138, Q139, Q140, Q141, Q142, Q143, Q144, Q145, Q146, Q147, Q148, Q149, Q150, Q151]), "depth" : 6 * mm, "offsetDistance" : 25 * mm});
        }
        {
            var Q0;
            Q0 = qSketchRegion(id + "F3", true);
            var Q1;
            Q1=sQuery(id+"F3.wireOp",EDGE,"E11");
            revolve(context, id + "F7", {"operationType" : NewBodyOperationType.INTERSECT, "surfaceOperationType" : NewSurfaceOperationType.NEW, "entities" : qUnion([Q0]), "axis" : qUnion([Q1]), "revolveType" : RevolveType.FULL});
        }
        {
            var Q0;
            {var subQ16=sQuery(id+"F0.wireOp",EDGE,"E8.MirrorCS");var subQ17=sQuery(id+"F0.wireOp",EDGE,"E6");var subQ19=sQuery(id+"F0.wireOp",EDGE,"E5");var subQ20=makeQuery(id+"F2.opExtrude","SWEPT_FACE",FACE,{"disambiguationData":[OSD([subQ19])]});var subQ21=sQuery(id+"F0.wireOp",EDGE,"E7.MirrorCS");var subQ25=sQuery(id+"F1.wireOp",EDGE,"E10");var subQ59=makeQuery(id+"F2.opExtrude","CAP_FACE",FACE,{"disambiguationData":[OSD([subQ19,subQ17,subQ21,subQ16,sQuery(id+"F0.wireOp",EDGE,"E9")])],"isStart":false});Q0=makeQuery(id+"F6.boolean.opBoolean","SPLIT",FACE,{"disambiguationData":[TD([subQ20])],"derivedFrom":makeQuery(id+"F4.boolean.opBoolean","MERGE",FACE,{"derivedFrom":[subQ59,makeQuery(id+"F2.opExtrude","CAP_FACE",FACE,{"disambiguationData":[OSD([subQ25])],"isStart":false}),makeQuery(id+"F4.opPattern","COPY",FACE,{"derivedFrom":subQ59,"instanceName":"1"}),makeQuery(id+"F4.opPattern","COPY",FACE,{"derivedFrom":subQ59,"instanceName":"2"}),makeQuery(id+"F4.opPattern","COPY",FACE,{"derivedFrom":subQ59,"instanceName":"3"}),makeQuery(id+"F4.opPattern","COPY",FACE,{"derivedFrom":subQ59,"instanceName":"4"}),makeQuery(id+"F4.opPattern","COPY",FACE,{"derivedFrom":subQ59,"instanceName":"5"}),makeQuery(id+"F4.opPattern","COPY",FACE,{"derivedFrom":subQ59,"instanceName":"6"}),makeQuery(id+"F4.opPattern","COPY",FACE,{"derivedFrom":subQ59,"instanceName":"7"}),makeQuery(id+"F4.opPattern","COPY",FACE,{"derivedFrom":subQ59,"instanceName":"8"}),makeQuery(id+"F4.opPattern","COPY",FACE,{"derivedFrom":subQ59,"instanceName":"9"}),makeQuery(id+"F4.opPattern","COPY",FACE,{"derivedFrom":subQ59,"instanceName":"10"}),makeQuery(id+"F4.opPattern","COPY",FACE,{"derivedFrom":subQ59,"instanceName":"11"}),makeQuery(id+"F4.opPattern","COPY",FACE,{"derivedFrom":subQ59,"instanceName":"12"}),makeQuery(id+"F4.opPattern","COPY",FACE,{"derivedFrom":subQ59,"instanceName":"13"}),makeQuery(id+"F4.opPattern","COPY",FACE,{"derivedFrom":subQ59,"instanceName":"14"}),makeQuery(id+"F4.opPattern","COPY",FACE,{"derivedFrom":subQ59,"instanceName":"15"}),makeQuery(id+"F4.opPattern","COPY",FACE,{"derivedFrom":subQ59,"instanceName":"16"}),makeQuery(id+"F4.opPattern","COPY",FACE,{"derivedFrom":subQ59,"instanceName":"17"})]})});}
            cPlane(context, id + "F8", {"entities" : qUnion([Q0]), "cplaneType" : CPlaneType.OFFSET, "offset" : 0 * mm, "width" : 150 * mm, "height" : 150 * mm});
        }
        {
            var Q0;
            Q0=qCreatedBy(makeId("Top.planeOp"),FACE);
            var sketch = newSketch(context, id + "F9", { "sketchPlane" : qUnion([Q0])});
            skFitSpline(sketch, "E169", {"points": [v(-8.15, -11.01) * mm, v(-8.06, -11.01) * mm, v(-7.98, -11.03) * mm, v(-7.91, -11.06) * mm]});
            skFitSpline(sketch, "E170", {"points": [v(-7.91, -11.06) * mm, v(-7.84, -11.1) * mm, v(-7.78, -11.14) * mm, v(-7.72, -11.2) * mm]});
            skFitSpline(sketch, "E171", {"points": [v(-7.72, -11.2) * mm, v(-7.66, -11.25) * mm, v(-7.62, -11.31) * mm, v(-7.59, -11.39) * mm]});
            skFitSpline(sketch, "E172", {"points": [v(-7.59, -11.39) * mm, v(-7.56, -11.46) * mm, v(-7.54, -11.54) * mm, v(-7.54, -11.62) * mm]});
            skFitSpline(sketch, "E173", {"points": [v(-5.37, -11.01) * mm, v(-5.28, -11.01) * mm, v(-5.2, -11.03) * mm, v(-5.13, -11.06) * mm]});
            skFitSpline(sketch, "E174", {"points": [v(-5.13, -11.06) * mm, v(-5.06, -11.1) * mm, v(-5, -11.14) * mm, v(-4.94, -11.2) * mm]});
            skFitSpline(sketch, "E175", {"points": [v(-4.94, -11.2) * mm, v(-4.88, -11.25) * mm, v(-4.84, -11.31) * mm, v(-4.81, -11.39) * mm]});
            skFitSpline(sketch, "E176", {"points": [v(-4.81, -11.39) * mm, v(-4.78, -11.46) * mm, v(-4.76, -11.54) * mm, v(-4.76, -11.62) * mm]});
            skLineSegment(sketch, "E177", {"start": v(-7.54, -11.62) * mm, "end": v(-7.54, -13.44) * mm});
            skLineSegment(sketch, "E178", {"start": v(-7.54, -13.44) * mm, "end": v(-8.18, -13.44) * mm});
            skLineSegment(sketch, "E179", {"start": v(-8.18, -13.44) * mm, "end": v(-8.18, -11.65) * mm});
            skLineSegment(sketch, "E180", {"start": v(-8.18, -11.65) * mm, "end": v(-9.36, -11.65) * mm});
            skLineSegment(sketch, "E181", {"start": v(-9.36, -11.65) * mm, "end": v(-9.36, -13.44) * mm});
            skLineSegment(sketch, "E182", {"start": v(-9.36, -13.44) * mm, "end": v(-10, -13.44) * mm});
            skLineSegment(sketch, "E183", {"start": v(-10, -13.44) * mm, "end": v(-10, -10.22) * mm});
            skLineSegment(sketch, "E184", {"start": v(-10, -10.22) * mm, "end": v(-9.36, -10.22) * mm});
            skLineSegment(sketch, "E185", {"start": v(-9.36, -10.22) * mm, "end": v(-9.36, -11.01) * mm});
            skLineSegment(sketch, "E186", {"start": v(-9.36, -11.01) * mm, "end": v(-8.15, -11.01) * mm});
            skFitSpline(sketch, "E187", {"points": [v(-6.61, -13.44) * mm, v(-6.7, -13.44) * mm, v(-6.78, -13.43) * mm, v(-6.85, -13.4) * mm]});
            skFitSpline(sketch, "E188", {"points": [v(-6.85, -13.4) * mm, v(-6.93, -13.36) * mm, v(-6.99, -13.32) * mm, v(-7.05, -13.26) * mm]});
            skFitSpline(sketch, "E189", {"points": [v(-7.05, -13.26) * mm, v(-7.1, -13.2) * mm, v(-7.14, -13.14) * mm, v(-7.18, -13.07) * mm]});
            skFitSpline(sketch, "E190", {"points": [v(-7.18, -13.07) * mm, v(-7.2, -13) * mm, v(-7.22, -12.92) * mm, v(-7.22, -12.83) * mm]});
            skLineSegment(sketch, "E191", {"start": v(-4.76, -11.62) * mm, "end": v(-4.76, -13.44) * mm});
            skLineSegment(sketch, "E192", {"start": v(-4.76, -13.44) * mm, "end": v(-6.61, -13.44) * mm});
            skLineSegment(sketch, "E193", {"start": v(-7.22, -12.83) * mm, "end": v(-7.22, -11.9) * mm});
            skLineSegment(sketch, "E194", {"start": v(-7.22, -11.9) * mm, "end": v(-5.4, -11.9) * mm});
            skLineSegment(sketch, "E195", {"start": v(-5.4, -11.9) * mm, "end": v(-5.4, -11.65) * mm});
            skLineSegment(sketch, "E196", {"start": v(-5.4, -11.65) * mm, "end": v(-7.22, -11.65) * mm});
            skLineSegment(sketch, "E197", {"start": v(-7.22, -11.65) * mm, "end": v(-7.22, -11.01) * mm});
            skLineSegment(sketch, "E198", {"start": v(-7.22, -11.01) * mm, "end": v(-5.37, -11.01) * mm});
            skLineSegment(sketch, "E199", {"start": v(-5.4, -12.47) * mm, "end": v(-6.58, -12.47) * mm});
            skLineSegment(sketch, "E200", {"start": v(-6.58, -12.47) * mm, "end": v(-6.58, -12.8) * mm});
            skLineSegment(sketch, "E201", {"start": v(-6.58, -12.8) * mm, "end": v(-5.4, -12.8) * mm});
            skLineSegment(sketch, "E202", {"start": v(-5.4, -12.8) * mm, "end": v(-5.4, -12.47) * mm});
            skFitSpline(sketch, "E203", {"points": [v(-3.86, -13.44) * mm, v(-3.95, -13.44) * mm, v(-4.03, -13.43) * mm, v(-4.1, -13.4) * mm]});
            skFitSpline(sketch, "E204", {"points": [v(-4.1, -13.4) * mm, v(-4.17, -13.36) * mm, v(-4.24, -13.32) * mm, v(-4.3, -13.26) * mm]});
            skFitSpline(sketch, "E205", {"points": [v(-4.3, -13.26) * mm, v(-4.35, -13.2) * mm, v(-4.4, -13.14) * mm, v(-4.43, -13.07) * mm]});
            skFitSpline(sketch, "E206", {"points": [v(-4.43, -13.07) * mm, v(-4.46, -13) * mm, v(-4.47, -12.92) * mm, v(-4.47, -12.83) * mm]});
            skLineSegment(sketch, "E207", {"start": v(-3.83, -11.65) * mm, "end": v(-3.83, -12.8) * mm});
            skLineSegment(sketch, "E208", {"start": v(-3.83, -12.8) * mm, "end": v(-2.01, -12.8) * mm});
            skLineSegment(sketch, "E209", {"start": v(-2.01, -12.8) * mm, "end": v(-2.01, -13.44) * mm});
            skLineSegment(sketch, "E210", {"start": v(-2.01, -13.44) * mm, "end": v(-3.86, -13.44) * mm});
            skFitSpline(sketch, "E211", {"points": [v(-4.47, -11.62) * mm, v(-4.47, -11.54) * mm, v(-4.46, -11.46) * mm, v(-4.43, -11.39) * mm]});
            skFitSpline(sketch, "E212", {"points": [v(-4.43, -11.39) * mm, v(-4.4, -11.31) * mm, v(-4.35, -11.25) * mm, v(-4.3, -11.2) * mm]});
            skFitSpline(sketch, "E213", {"points": [v(-4.3, -11.2) * mm, v(-4.24, -11.14) * mm, v(-4.17, -11.1) * mm, v(-4.1, -11.06) * mm]});
            skFitSpline(sketch, "E214", {"points": [v(-4.1, -11.06) * mm, v(-4.03, -11.03) * mm, v(-3.95, -11.01) * mm, v(-3.86, -11.01) * mm]});
            skLineSegment(sketch, "E215", {"start": v(-4.47, -12.83) * mm, "end": v(-4.47, -11.62) * mm});
            skLineSegment(sketch, "E216", {"start": v(-4.47, -11.62) * mm, "end": v(-4.47, -12.83) * mm});
            skLineSegment(sketch, "E217", {"start": v(-3.86, -11.01) * mm, "end": v(-2.01, -11.01) * mm});
            skLineSegment(sketch, "E218", {"start": v(-2.01, -11.01) * mm, "end": v(-2.01, -11.65) * mm});
            skLineSegment(sketch, "E219", {"start": v(-2.01, -11.65) * mm, "end": v(-3.83, -11.65) * mm});
            skLineSegment(sketch, "E220", {"start": v(0.76, -11.01) * mm, "end": v(0.76, -11.23) * mm});
            skLineSegment(sketch, "E221", {"start": v(0.76, -11.23) * mm, "end": v(-0.14, -12.23) * mm});
            skLineSegment(sketch, "E222", {"start": v(-0.14, -12.23) * mm, "end": v(0.76, -13.22) * mm});
            skLineSegment(sketch, "E223", {"start": v(0.76, -13.22) * mm, "end": v(0.76, -13.44) * mm});
            skLineSegment(sketch, "E224", {"start": v(0.76, -13.44) * mm, "end": v(0.12, -13.44) * mm});
            skLineSegment(sketch, "E225", {"start": v(0.12, -13.44) * mm, "end": v(-0.7, -12.55) * mm});
            skLineSegment(sketch, "E226", {"start": v(-0.7, -12.55) * mm, "end": v(-1.03, -12.55) * mm});
            skLineSegment(sketch, "E227", {"start": v(-1.03, -12.55) * mm, "end": v(-1.03, -13.44) * mm});
            skLineSegment(sketch, "E228", {"start": v(-1.03, -13.44) * mm, "end": v(-1.67, -13.44) * mm});
            skLineSegment(sketch, "E229", {"start": v(-1.67, -13.44) * mm, "end": v(-1.67, -10.22) * mm});
            skLineSegment(sketch, "E230", {"start": v(-1.67, -10.22) * mm, "end": v(-1.03, -10.22) * mm});
            skLineSegment(sketch, "E231", {"start": v(-1.03, -10.22) * mm, "end": v(-1.03, -11.9) * mm});
            skLineSegment(sketch, "E232", {"start": v(-1.03, -11.9) * mm, "end": v(-0.7, -11.9) * mm});
            skLineSegment(sketch, "E233", {"start": v(-0.7, -11.9) * mm, "end": v(0.12, -11.01) * mm});
            skLineSegment(sketch, "E234", {"start": v(0.12, -11.01) * mm, "end": v(0.76, -11.01) * mm});
            skLineSegment(sketch, "E235", {"start": v(1.67, -13.44) * mm, "end": v(1.03, -13.44) * mm});
            skLineSegment(sketch, "E236", {"start": v(1.03, -13.44) * mm, "end": v(1.03, -12.8) * mm});
            skLineSegment(sketch, "E237", {"start": v(1.03, -12.8) * mm, "end": v(1.67, -12.8) * mm});
            skLineSegment(sketch, "E238", {"start": v(1.67, -12.8) * mm, "end": v(1.67, -13.44) * mm});
            skFitSpline(sketch, "E239", {"points": [v(2, -11.62) * mm, v(2, -11.54) * mm, v(2.01, -11.46) * mm, v(2.04, -11.39) * mm]});
            skFitSpline(sketch, "E240", {"points": [v(2.04, -11.39) * mm, v(2.08, -11.31) * mm, v(2.12, -11.25) * mm, v(2.18, -11.2) * mm]});
            skFitSpline(sketch, "E241", {"points": [v(2.18, -11.2) * mm, v(2.23, -11.14) * mm, v(2.3, -11.1) * mm, v(2.37, -11.06) * mm]});
            skFitSpline(sketch, "E242", {"points": [v(2.37, -11.06) * mm, v(2.45, -11.03) * mm, v(2.53, -11.01) * mm, v(2.6, -11.01) * mm]});
            skLineSegment(sketch, "E243", {"start": v(3.95, -11.01) * mm, "end": v(3.95, -11.65) * mm});
            skLineSegment(sketch, "E244", {"start": v(3.95, -11.65) * mm, "end": v(2.64, -11.65) * mm});
            skLineSegment(sketch, "E245", {"start": v(2.64, -11.65) * mm, "end": v(2.64, -13.44) * mm});
            skLineSegment(sketch, "E246", {"start": v(2.64, -13.44) * mm, "end": v(2, -13.44) * mm});
            skLineSegment(sketch, "E247", {"start": v(2, -13.44) * mm, "end": v(2, -11.62) * mm});
            skLineSegment(sketch, "E248", {"start": v(2.6, -11.01) * mm, "end": v(3.95, -11.01) * mm});
            skLineSegment(sketch, "E249", {"start": v(3.95, -11.01) * mm, "end": v(2.6, -11.01) * mm});
            skFitSpline(sketch, "E250", {"points": [v(9.4, -11.01) * mm, v(9.48, -11.01) * mm, v(9.56, -11.03) * mm, v(9.63, -11.06) * mm]});
            skFitSpline(sketch, "E251", {"points": [v(9.63, -11.06) * mm, v(9.7, -11.1) * mm, v(9.77, -11.14) * mm, v(9.82, -11.2) * mm]});
            skFitSpline(sketch, "E252", {"points": [v(9.82, -11.2) * mm, v(9.88, -11.25) * mm, v(9.92, -11.31) * mm, v(9.95, -11.39) * mm]});
            skFitSpline(sketch, "E253", {"points": [v(9.95, -11.39) * mm, v(9.98, -11.46) * mm, v(10, -11.54) * mm, v(10, -11.62) * mm]});
            skLineSegment(sketch, "E254", {"start": v(7.33, -11.01) * mm, "end": v(6, -13.44) * mm});
            skLineSegment(sketch, "E255", {"start": v(6, -13.44) * mm, "end": v(5.44, -13.44) * mm});
            skLineSegment(sketch, "E256", {"start": v(5.44, -13.44) * mm, "end": v(4.1, -11.01) * mm});
            skLineSegment(sketch, "E257", {"start": v(4.1, -11.01) * mm, "end": v(4.84, -11.01) * mm});
            skLineSegment(sketch, "E258", {"start": v(4.84, -11.01) * mm, "end": v(5.72, -12.63) * mm});
            skLineSegment(sketch, "E259", {"start": v(5.72, -12.63) * mm, "end": v(6.6, -11.01) * mm});
            skLineSegment(sketch, "E260", {"start": v(6.6, -11.01) * mm, "end": v(7.33, -11.01) * mm});
            skFitSpline(sketch, "E261", {"points": [v(8.15, -13.44) * mm, v(8.06, -13.44) * mm, v(7.98, -13.43) * mm, v(7.9, -13.4) * mm]});
            skFitSpline(sketch, "E262", {"points": [v(7.9, -13.4) * mm, v(7.84, -13.36) * mm, v(7.77, -13.32) * mm, v(7.72, -13.26) * mm]});
            skFitSpline(sketch, "E263", {"points": [v(7.72, -13.26) * mm, v(7.66, -13.2) * mm, v(7.62, -13.14) * mm, v(7.59, -13.07) * mm]});
            skFitSpline(sketch, "E264", {"points": [v(7.59, -13.07) * mm, v(7.55, -13) * mm, v(7.54, -12.92) * mm, v(7.54, -12.83) * mm]});
            skLineSegment(sketch, "E265", {"start": v(10, -11.62) * mm, "end": v(10, -13.44) * mm});
            skLineSegment(sketch, "E266", {"start": v(10, -13.44) * mm, "end": v(8.15, -13.44) * mm});
            skLineSegment(sketch, "E267", {"start": v(7.54, -12.83) * mm, "end": v(7.54, -11.9) * mm});
            skLineSegment(sketch, "E268", {"start": v(7.54, -11.9) * mm, "end": v(9.36, -11.9) * mm});
            skLineSegment(sketch, "E269", {"start": v(9.36, -11.9) * mm, "end": v(9.36, -11.65) * mm});
            skLineSegment(sketch, "E270", {"start": v(9.36, -11.65) * mm, "end": v(7.54, -11.65) * mm});
            skLineSegment(sketch, "E271", {"start": v(7.54, -11.65) * mm, "end": v(7.54, -11.01) * mm});
            skLineSegment(sketch, "E272", {"start": v(7.54, -11.01) * mm, "end": v(9.4, -11.01) * mm});
            skLineSegment(sketch, "E273", {"start": v(9.36, -12.47) * mm, "end": v(8.18, -12.47) * mm});
            skLineSegment(sketch, "E274", {"start": v(8.18, -12.47) * mm, "end": v(8.18, -12.8) * mm});
            skLineSegment(sketch, "E275", {"start": v(8.18, -12.8) * mm, "end": v(9.36, -12.8) * mm});
            skLineSegment(sketch, "E276", {"start": v(9.36, -12.8) * mm, "end": v(9.36, -12.47) * mm});
            skSolve(sketch);
        }
        {
            var Q0;
            Q0 = qSketchRegion(id + "F9", true);
            extrude(context, id + "F10", {"entities" : qUnion([Q0]), "operationType" : NewBodyOperationType.ADD, "depth" : 7 * mm, "offsetDistance" : 25 * mm});
        }
        {
            var Q0;
            Q0=qCreatedBy(makeId("Front.planeOp"),FACE);
            var sketch = newSketch(context, id + "F11", { "sketchPlane" : qUnion([Q0])});
            skLineSegment(sketch, "E277", {"start": v(-17.4, 6.4) * mm, "end": v(-14.36, 6.4) * mm});
            skLineSegment(sketch, "E278", {"start": v(-14.36, 6.4) * mm, "end": v(0, 3.4) * mm});
            skLineSegment(sketch, "E279", {"start": v(0, 3.4) * mm, "end": v(0, 9.4) * mm});
            skLineSegment(sketch, "E280", {"start": v(0, 9.4) * mm, "end": v(-17.4, 9.4) * mm});
            skLineSegment(sketch, "E281", {"start": v(-17.4, 9.4) * mm, "end": v(-17.4, 6.4) * mm});
            skSolve(sketch);
        }
        {
            var Q0;
            Q0 = qSketchRegion(id + "F11", true);
            var Q1;
            Q1=sQuery(id+"F11.wireOp",EDGE,"E279");
            revolve(context, id + "F12", {"operationType" : NewBodyOperationType.REMOVE, "surfaceOperationType" : NewSurfaceOperationType.NEW, "entities" : qUnion([Q0]), "axis" : qUnion([Q1]), "revolveType" : RevolveType.FULL, "oppositeDirection" : true});
        }
    });
